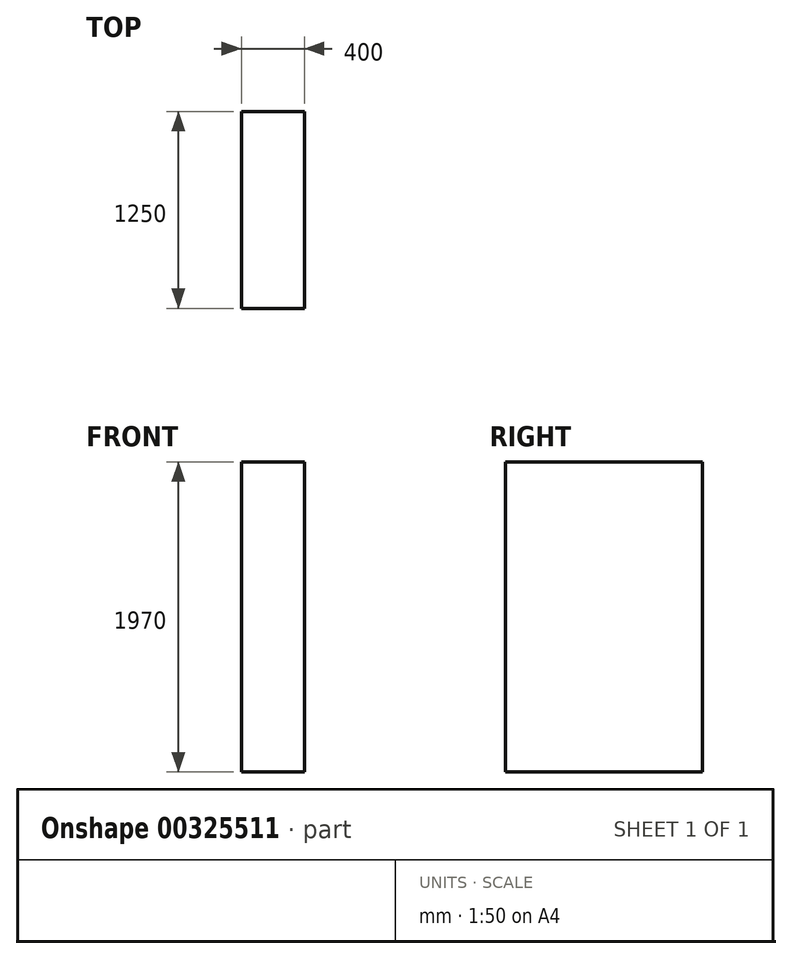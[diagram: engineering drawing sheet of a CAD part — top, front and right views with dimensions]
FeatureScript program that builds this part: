
annotation { "Feature Type Name" : "Feature", "Feature Type Description" : "" }
export const myFeature = defineFeature(function(context is Context, id is Id, definition is map)
    precondition{}
    {
        {
            var Q0;
            Q0=qCreatedBy(makeId("Top.planeOp"),FACE);
            var sketch = newSketch(context, id + "F0", { "sketchPlane" : qUnion([Q0])});
            skLineSegment(sketch, "E0.bottom", {"start": v(200, -625) * mm, "end": v(-200, -625) * mm});
            skLineSegment(sketch, "E0.top", {"start": v(200, 625) * mm, "end": v(-200, 625) * mm});
            skLineSegment(sketch, "E0.left", {"start": v(200, -625) * mm, "end": v(200, 625) * mm});
            skLineSegment(sketch, "E0.right", {"start": v(-200, -625) * mm, "end": v(-200, 625) * mm});
            skPoint(sketch, "E0.middle", {"position": v(0, 0) * mm});
            skSolve(sketch);
        }
        {
            var Q0;
            Q0 = qSketchRegion(id + "F0", true);
            extrude(context, id + "F1", {"entities" : qUnion([Q0]), "depth" : 1970 * mm});
        }
    });
